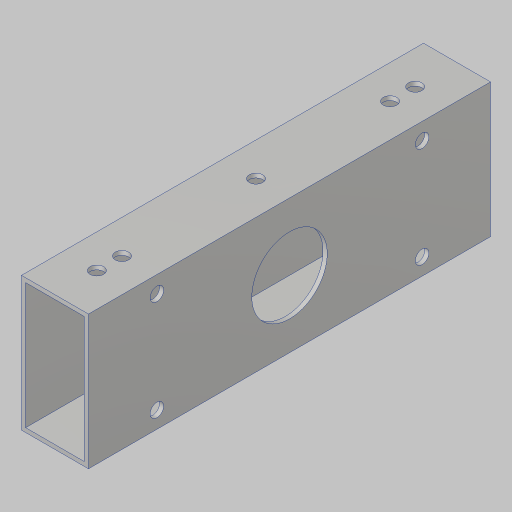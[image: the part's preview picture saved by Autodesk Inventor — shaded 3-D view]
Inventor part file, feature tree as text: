
AUTODESK INVENTOR PART (.ipt)
format: ipt  version: 2023.5 (Build 275446000, 446)  size: 172,032 bytes
history: native  units: in
note: dims shown in document units (in); Inventor stores cm internally (conversion verified against a paired STEP export)
features: sketch x5, hole x4, extrude x2, projected_geometry x2
ambient origin geometry x8: Origin, YZ Plane, XZ Plane, XY Plane, X Axis, Y Axis, Z Axis, Center Point
bodies: Solid1 (feature_tree)
feature tree (13):
  extrude  "Extrusion1"  Depth=4.0in
  hole  "Hole1"  [1 undecoded]
  hole  "Hole3"  [1 undecoded]
  hole  "Hole4"  [1 undecoded]
  extrude  "Extrusion2"  Depth=1.0in
  hole  "Hole2"  [1 undecoded]
  sketch  "Sketch2"  dims[d4=0.0in d5=4.0in]
  projected_geometry  "Projected Loop1"
  sketch  "Sketch3"  dims[d6=0.201in d7=0.75in d8=0.385in d9=0.25in d10=0.5635in d11=1.0in d12=0.8108in d14=4.7244in]
  sketch  "Sketch4"  dims[d15=3.7402in d16=4.2323in]
  sketch  "Sketch5"  dims[d17=1.5in]
  sketch  "Sketch6"  dims[d18=0.156in d19=0.38in d20=0.375in d21=0.25in d22=0.5635in d23=1.0in d24=0.8108in d25=4.2323in d28=1.5in d29=0.201in d30=0.38in d31=0.385in d32=0.25in d33=0.5635in d34=1.0in d35=0.8108in d36=4.75in d37=0.201in d38=0.75in d39=0.385in d40=0.25in d41=0.5635in d42=1.0in d43=0.8108in d44=1.125in d45=0.0in d46=0.0in]
  projected_geometry  "Projected Loop2"
note: 4 required parameter values undecoded (feature->parameter linkage not recoverable at this tier; creation-order binding heuristic only, values carry confidence <= 0.55)
